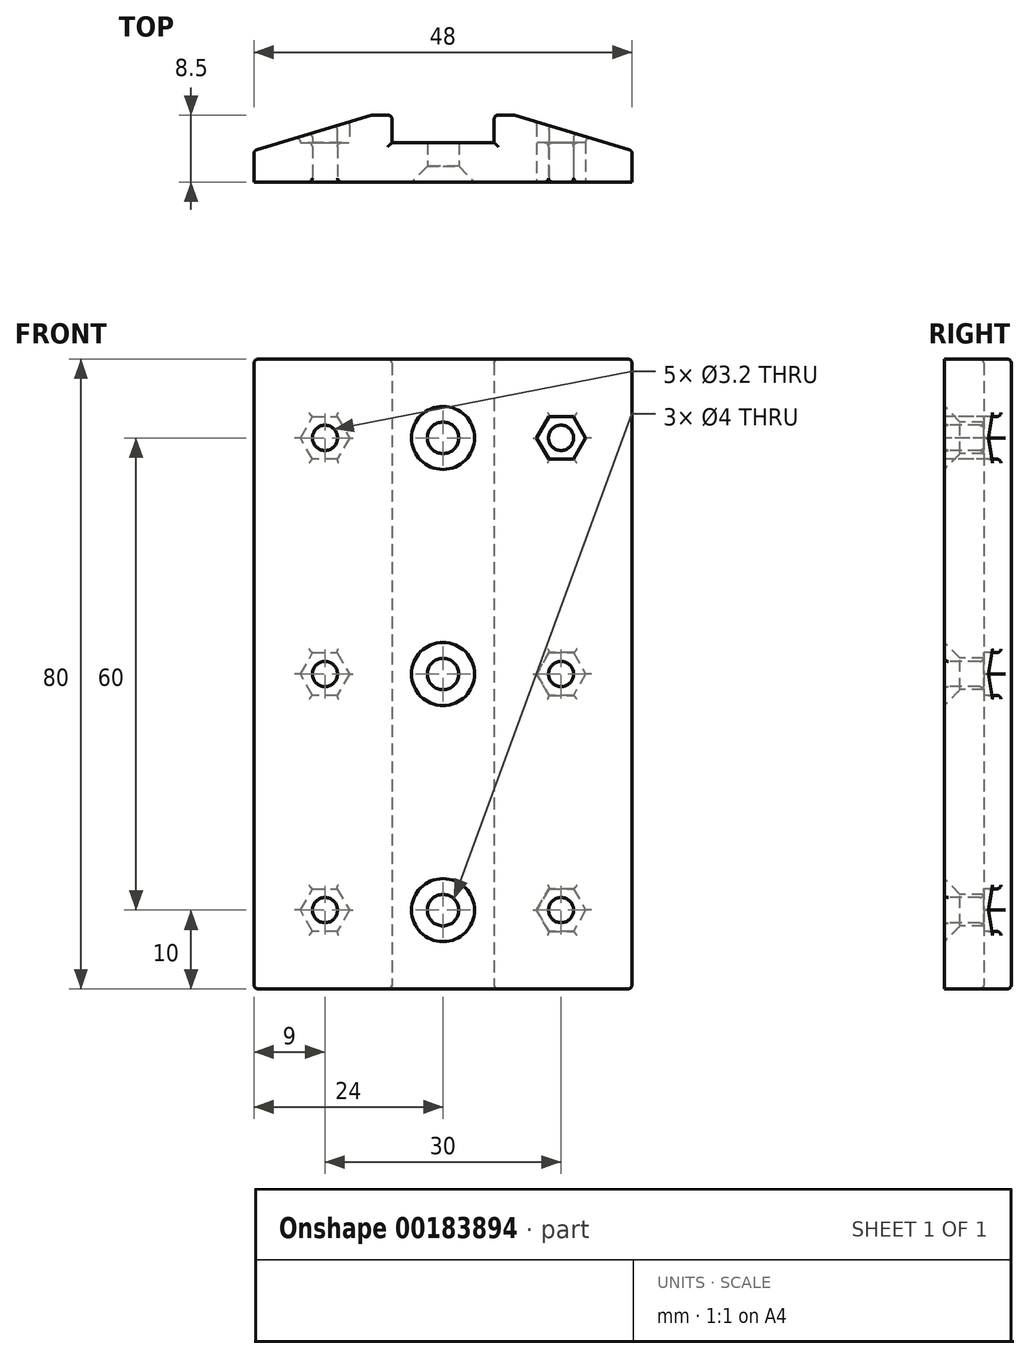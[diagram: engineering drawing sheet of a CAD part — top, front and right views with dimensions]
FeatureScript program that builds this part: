
annotation { "Feature Type Name" : "Feature", "Feature Type Description" : "" }
export const myFeature = defineFeature(function(context is Context, id is Id, definition is map)
    precondition{}
    {
        {
            var Q0;
            Q0=qCreatedBy(makeId("Front.planeOp"),FACE);
            var sketch = newSketch(context, id + "F0", { "sketchPlane" : qUnion([Q0])});
            skLineSegment(sketch, "E0.bottom", {"start": v(6, -40) * mm, "end": v(-6, -40) * mm});
            skLineSegment(sketch, "E0.top", {"start": v(6, 40) * mm, "end": v(-6, 40) * mm});
            skLineSegment(sketch, "E0.left", {"start": v(6, -40) * mm, "end": v(6, 40) * mm});
            skLineSegment(sketch, "E0.right", {"start": v(-6, -40) * mm, "end": v(-6, 40) * mm});
            skPoint(sketch, "E0.middle", {"position": v(0, 0) * mm});
            skCircle(sketch, "E1", {"center": v(0, -30) * mm, "radius": 2 * mm});
            skCircle(sketch, "E2.1.0.0", {"center": v(0, 0) * mm, "radius": 2 * mm});
            skCircle(sketch, "E2.2.0.0", {"center": v(0, 30) * mm, "radius": 2 * mm});
            skLineSegment(sketch, "E2.direction1", {"start": v(0, -30) * mm, "end": v(0, 0) * mm, "construction": true});
            skLineSegment(sketch, "E3.bottom", {"start": v(-6, 40) * mm, "end": v(-24, 40) * mm});
            skLineSegment(sketch, "E3.top", {"start": v(-6, -40) * mm, "end": v(-24, -40) * mm});
            skLineSegment(sketch, "E3.left", {"start": v(-6, 40) * mm, "end": v(-6, -40) * mm});
            skLineSegment(sketch, "E3.right", {"start": v(-24, 40) * mm, "end": v(-24, -40) * mm});
            skLineSegment(sketch, "E4.MirrorCS", {"start": v(6, 40) * mm, "end": v(24, 40) * mm});
            skLineSegment(sketch, "E5.MirrorCS", {"start": v(24, 40) * mm, "end": v(24, -40) * mm});
            skLineSegment(sketch, "E6.MirrorCS", {"start": v(6, -40) * mm, "end": v(24, -40) * mm});
            skLineSegment(sketch, "E7.0", {"start": v(-6.5, 40) * mm, "end": v(-6.5, -40) * mm});
            skLineSegment(sketch, "E8.MirrorCS", {"start": v(6.5, 40) * mm, "end": v(6.5, -40) * mm});
            skCircle(sketch, "E9", {"center": v(-15, 30) * mm, "radius": 1.6 * mm});
            skCircle(sketch, "E10.cCircle", {"center": v(-15, 30) * mm, "radius": 2.7 * mm, "construction": true});
            skLineSegment(sketch, "E10.0", {"start": v(-16.56, 32.7) * mm, "end": v(-13.44, 32.7) * mm});
            skLineSegment(sketch, "E10.1", {"start": v(-13.44, 32.7) * mm, "end": v(-11.88, 30) * mm});
            skLineSegment(sketch, "E10.2", {"start": v(-11.88, 30) * mm, "end": v(-13.44, 27.3) * mm});
            skLineSegment(sketch, "E10.3", {"start": v(-13.44, 27.3) * mm, "end": v(-16.56, 27.3) * mm});
            skLineSegment(sketch, "E10.4", {"start": v(-16.56, 27.3) * mm, "end": v(-18.12, 30) * mm});
            skLineSegment(sketch, "E10.5", {"start": v(-18.12, 30) * mm, "end": v(-16.56, 32.7) * mm});
            skPoint(sketch, "E10.0.midPoint", {"position": v(-15, 32.7) * mm});
            skLineSegment(sketch, "E11", {"start": v(-15, 40) * mm, "end": v(-15, -40) * mm, "construction": true});
            skLineSegment(sketch, "E12", {"start": v(-24, 30) * mm, "end": v(24, 30) * mm, "construction": true});
            skLineSegment(sketch, "E13", {"start": v(-24, 0) * mm, "end": v(24, 0) * mm, "construction": true});
            skLineSegment(sketch, "E14", {"start": v(-24, -30) * mm, "end": v(24, -30) * mm, "construction": true});
            skCircle(sketch, "E15.cCircle", {"center": v(-15, 0) * mm, "radius": 2.7 * mm, "construction": true});
            skLineSegment(sketch, "E15.0", {"start": v(-16.56, 2.7) * mm, "end": v(-13.44, 2.7) * mm});
            skLineSegment(sketch, "E15.1", {"start": v(-13.44, 2.7) * mm, "end": v(-11.88, 0) * mm});
            skLineSegment(sketch, "E15.2", {"start": v(-11.88, 0) * mm, "end": v(-13.44, -2.7) * mm});
            skLineSegment(sketch, "E15.3", {"start": v(-13.44, -2.7) * mm, "end": v(-16.56, -2.7) * mm});
            skLineSegment(sketch, "E15.4", {"start": v(-16.56, -2.7) * mm, "end": v(-18.12, 0) * mm});
            skLineSegment(sketch, "E15.5", {"start": v(-18.12, 0) * mm, "end": v(-16.56, 2.7) * mm});
            skPoint(sketch, "E15.0.midPoint", {"position": v(-15, 2.7) * mm});
            skCircle(sketch, "E16.cCircle", {"center": v(-15, -30) * mm, "radius": 2.7 * mm, "construction": true});
            skLineSegment(sketch, "E16.0", {"start": v(-16.56, -27.3) * mm, "end": v(-13.44, -27.3) * mm});
            skLineSegment(sketch, "E16.1", {"start": v(-13.44, -27.3) * mm, "end": v(-11.88, -30) * mm});
            skLineSegment(sketch, "E16.2", {"start": v(-11.88, -30) * mm, "end": v(-13.44, -32.7) * mm});
            skLineSegment(sketch, "E16.3", {"start": v(-13.44, -32.7) * mm, "end": v(-16.56, -32.7) * mm});
            skLineSegment(sketch, "E16.4", {"start": v(-16.56, -32.7) * mm, "end": v(-18.12, -30) * mm});
            skLineSegment(sketch, "E16.5", {"start": v(-18.12, -30) * mm, "end": v(-16.56, -27.3) * mm});
            skPoint(sketch, "E16.0.midPoint", {"position": v(-15, -27.3) * mm});
            skCircle(sketch, "E17", {"center": v(-15, 0) * mm, "radius": 1.6 * mm});
            skCircle(sketch, "E18", {"center": v(-15, -30) * mm, "radius": 1.6 * mm});
            skLineSegment(sketch, "E19", {"start": v(0, 30) * mm, "end": v(0, 0) * mm, "construction": true});
            skCircle(sketch, "E20.MirrorC", {"center": v(15, 30) * mm, "radius": 1.6 * mm});
            skLineSegment(sketch, "E21.MirrorCS", {"start": v(11.88, 30) * mm, "end": v(13.44, 27.3) * mm});
            skLineSegment(sketch, "E22.MirrorCS", {"start": v(13.44, 27.3) * mm, "end": v(16.56, 27.3) * mm});
            skLineSegment(sketch, "E23.MirrorCS", {"start": v(16.56, 27.3) * mm, "end": v(18.12, 30) * mm});
            skLineSegment(sketch, "E24.MirrorCS", {"start": v(18.12, 30) * mm, "end": v(16.56, 32.7) * mm});
            skLineSegment(sketch, "E25.MirrorCS", {"start": v(13.44, 32.7) * mm, "end": v(11.88, 30) * mm});
            skLineSegment(sketch, "E26.MirrorCS", {"start": v(16.56, 32.7) * mm, "end": v(13.44, 32.7) * mm});
            skLineSegment(sketch, "E27.MirrorCS", {"start": v(13.44, 2.7) * mm, "end": v(11.88, 0) * mm});
            skLineSegment(sketch, "E28.MirrorCS", {"start": v(16.56, 2.7) * mm, "end": v(13.44, 2.7) * mm});
            skCircle(sketch, "E29.MirrorC", {"center": v(15, 0) * mm, "radius": 1.6 * mm});
            skLineSegment(sketch, "E30.MirrorCS", {"start": v(18.12, 0) * mm, "end": v(16.56, 2.7) * mm});
            skLineSegment(sketch, "E31.MirrorCS", {"start": v(16.56, -2.7) * mm, "end": v(18.12, 0) * mm});
            skLineSegment(sketch, "E32.MirrorCS", {"start": v(13.44, -2.7) * mm, "end": v(16.56, -2.7) * mm});
            skLineSegment(sketch, "E33.MirrorCS", {"start": v(11.88, 0) * mm, "end": v(13.44, -2.7) * mm});
            skLineSegment(sketch, "E34.MirrorCS", {"start": v(11.88, -30) * mm, "end": v(13.44, -32.7) * mm});
            skLineSegment(sketch, "E35.MirrorCS", {"start": v(13.44, -27.3) * mm, "end": v(11.88, -30) * mm});
            skLineSegment(sketch, "E36.MirrorCS", {"start": v(16.56, -27.3) * mm, "end": v(13.44, -27.3) * mm});
            skLineSegment(sketch, "E37.MirrorCS", {"start": v(18.12, -30) * mm, "end": v(16.56, -27.3) * mm});
            skLineSegment(sketch, "E38.MirrorCS", {"start": v(16.56, -32.7) * mm, "end": v(18.12, -30) * mm});
            skLineSegment(sketch, "E39.MirrorCS", {"start": v(13.44, -32.7) * mm, "end": v(16.56, -32.7) * mm});
            skCircle(sketch, "E40.MirrorC", {"center": v(15, -30) * mm, "radius": 1.6 * mm});
            skSolve(sketch);
        }
        {
            var Q0;
            Q0 = qSketchRegion(id + "F0", true);
            var Q1;
            Q1=makeQuery(id+"F0.imprint","IMPRINT",FACE,{"disambiguationData":[TD([[makeQuery(id+"F0.imprint","IMPRINT",EDGE,{"derivedFrom":sQuery(id+"F0.wireOp",EDGE,"E2.2.0.0")}),1.0]])]});
            var Q2;
            Q2=makeQuery(id+"F0.imprint","IMPRINT",FACE,{"disambiguationData":[TD([[makeQuery(id+"F0.imprint","IMPRINT",EDGE,{"derivedFrom":sQuery(id+"F0.wireOp",EDGE,"E2.1.0.0")}),1.0]])]});
            var Q3;
            Q3=makeQuery(id+"F0.imprint","IMPRINT",FACE,{"disambiguationData":[TD([[makeQuery(id+"F0.imprint","IMPRINT",EDGE,{"derivedFrom":sQuery(id+"F0.wireOp",EDGE,"E1")}),1.0]])]});
            extrude(context, id + "F1", {"entities" : qUnion([Q0, Q1, Q2, Q3]), "oppositeDirection" : true, "depth" : 5 * mm});
        }
        {
            var Q0;
            {var subQ0=sQuery(id+"F0.wireOp",EDGE,"E3.right");Q0=makeQuery(id+"F0.imprint","IMPRINT",FACE,{"disambiguationData":[TD([[makeQuery(id+"F0.imprint","IMPRINT",EDGE,{"derivedFrom":subQ0}),1.0]])]});}
            var Q1;
            {var subQ0=sQuery(id+"F0.wireOp",EDGE,"E5.MirrorCS");Q1=makeQuery(id+"F0.imprint","IMPRINT",FACE,{"disambiguationData":[TD([[makeQuery(id+"F0.imprint","IMPRINT",EDGE,{"derivedFrom":subQ0}),-1.0]])]});}
            extrude(context, id + "F2", {"entities" : qUnion([Q0, Q1]), "operationType" : NewBodyOperationType.ADD, "oppositeDirection" : true, "depth" : 8.5 * mm});
        }
        {
            var Q0;
            Q0=makeQuery(id+"F2.opExtrude","CAP_EDGE",EDGE,{"disambiguationData":[OSD([sQuery(id+"F0.wireOp",EDGE,"E3.right")])],"isStart":false});
            chamfer(context, id + "F3", {"entities" : qUnion([Q0]), "chamferType" : ChamferType.TWO_OFFSETS, "width1" : 4.5 * mm, "oppositeDirection" : false, "width2" : 15 * mm});
        }
        {
            var Q0;
            Q0=makeQuery(id+"F2.opExtrude","CAP_EDGE",EDGE,{"disambiguationData":[OSD([sQuery(id+"F0.wireOp",EDGE,"E5.MirrorCS")])],"isStart":false});
            chamfer(context, id + "F4", {"entities" : qUnion([Q0]), "chamferType" : ChamferType.TWO_OFFSETS, "width1" : 4.5 * mm, "oppositeDirection" : true, "width2" : 15 * mm, "tangentPropagation" : true});
        }
        {
            var Q0;
            Q0=sQuery(id+"F0.wireOp",VERTEX,"E2.2.0.0.center");
            var Q1;
            Q1=sQuery(id+"F0.wireOp",VERTEX,"E0.middle");
            var Q2;
            Q2=sQuery(id+"F0.wireOp",VERTEX,"E2.direction1.start");
            var Q3;
            Q3=makeQuery(id+"F1.opExtrude","SWEPT_BODY",BODY,{"disambiguationData":[OSD([sQuery(id+"F0.wireOp",EDGE,"E0.bottom"),sQuery(id+"F0.wireOp",EDGE,"E0.top"),sQuery(id+"F0.wireOp",EDGE,"E3.bottom"),sQuery(id+"F0.wireOp",EDGE,"E3.top"),sQuery(id+"F0.wireOp",EDGE,"E3.right"),sQuery(id+"F0.wireOp",EDGE,"E4.MirrorCS"),sQuery(id+"F0.wireOp",EDGE,"E5.MirrorCS"),sQuery(id+"F0.wireOp",EDGE,"E6.MirrorCS")])]});
            hole(context, id + "F5", {"style" : HoleStyle.C_SINK, "endStyle" : HoleEndStyle.THROUGH, "holeDiameter" : 4 * mm, "cSinkDiameter" : 8 * mm, "cSinkAngle" : 90 * degree, "locations" : qUnion([Q0, Q1, Q2]), "scope" : qUnion([Q3]), "isTappedThrough" : true});
        }
        {
            var Q0;
            Q0=makeQuery(id+"F0.imprint","IMPRINT",FACE,{"disambiguationData":[TD([[makeQuery(id+"F0.imprint","IMPRINT",EDGE,{"derivedFrom":sQuery(id+"F0.wireOp",EDGE,"E20.MirrorC")}),1.0]])]});
            var Q1;
            Q1=makeQuery(id+"F0.imprint","IMPRINT",FACE,{"disambiguationData":[TD([[makeQuery(id+"F0.imprint","IMPRINT",EDGE,{"derivedFrom":sQuery(id+"F0.wireOp",EDGE,"E27.MirrorCS")}),1.0]])]});
            var Q2;
            Q2=makeQuery(id+"F0.imprint","IMPRINT",FACE,{"disambiguationData":[TD([[makeQuery(id+"F0.imprint","IMPRINT",EDGE,{"derivedFrom":sQuery(id+"F0.wireOp",EDGE,"E9")}),-1.0]])]});
            var Q3;
            Q3=makeQuery(id+"F0.imprint","IMPRINT",FACE,{"disambiguationData":[TD([[makeQuery(id+"F0.imprint","IMPRINT",EDGE,{"derivedFrom":sQuery(id+"F0.wireOp",EDGE,"E15.0")}),-1.0]])]});
            var Q4;
            Q4=makeQuery(id+"F0.imprint","IMPRINT",FACE,{"disambiguationData":[TD([[makeQuery(id+"F0.imprint","IMPRINT",EDGE,{"derivedFrom":sQuery(id+"F0.wireOp",EDGE,"E16.0")}),-1.0]])]});
            var Q5;
            Q5=makeQuery(id+"F0.imprint","IMPRINT",FACE,{"disambiguationData":[TD([[makeQuery(id+"F0.imprint","IMPRINT",EDGE,{"derivedFrom":sQuery(id+"F0.wireOp",EDGE,"E34.MirrorCS")}),1.0]])]});
            extrude(context, id + "F6", {"entities" : qUnion([Q0, Q1, Q2, Q3, Q4, Q5]), "operationType" : NewBodyOperationType.ADD, "oppositeDirection" : true, "depth" : 5 * mm});
        }
        {
            var Q0;
            Q0=makeQuery(id+"F4.opChamfer","BLEND_FACE",FACE,{"disambiguationData":[OSD([sQuery(id+"F0.wireOp",EDGE,"E5.MirrorCS")])]});
            var Q1;
            Q1=makeQuery(id+"F2.opExtrude","CAP_FACE",FACE,{"disambiguationData":[OSD([sQuery(id+"F0.wireOp",EDGE,"E4.MirrorCS"),sQuery(id+"F0.wireOp",EDGE,"E5.MirrorCS"),sQuery(id+"F0.wireOp",EDGE,"E6.MirrorCS"),sQuery(id+"F0.wireOp",EDGE,"E8.MirrorCS"),sQuery(id+"F0.wireOp",EDGE,"E21.MirrorCS"),sQuery(id+"F0.wireOp",EDGE,"E22.MirrorCS"),sQuery(id+"F0.wireOp",EDGE,"E23.MirrorCS"),sQuery(id+"F0.wireOp",EDGE,"E24.MirrorCS"),sQuery(id+"F0.wireOp",EDGE,"E25.MirrorCS"),sQuery(id+"F0.wireOp",EDGE,"E26.MirrorCS"),sQuery(id+"F0.wireOp",EDGE,"E27.MirrorCS"),sQuery(id+"F0.wireOp",EDGE,"E28.MirrorCS"),sQuery(id+"F0.wireOp",EDGE,"E30.MirrorCS"),sQuery(id+"F0.wireOp",EDGE,"E31.MirrorCS"),sQuery(id+"F0.wireOp",EDGE,"E32.MirrorCS"),sQuery(id+"F0.wireOp",EDGE,"E33.MirrorCS"),sQuery(id+"F0.wireOp",EDGE,"E34.MirrorCS"),sQuery(id+"F0.wireOp",EDGE,"E35.MirrorCS"),sQuery(id+"F0.wireOp",EDGE,"E36.MirrorCS"),sQuery(id+"F0.wireOp",EDGE,"E37.MirrorCS"),sQuery(id+"F0.wireOp",EDGE,"E38.MirrorCS"),sQuery(id+"F0.wireOp",EDGE,"E39.MirrorCS")])],"isStart":false});
            var Q2;
            Q2=makeQuery(id+"F2.opExtrude","CAP_FACE",FACE,{"disambiguationData":[OSD([sQuery(id+"F0.wireOp",EDGE,"E3.bottom"),sQuery(id+"F0.wireOp",EDGE,"E3.top"),sQuery(id+"F0.wireOp",EDGE,"E3.right"),sQuery(id+"F0.wireOp",EDGE,"E7.0"),sQuery(id+"F0.wireOp",EDGE,"E10.0"),sQuery(id+"F0.wireOp",EDGE,"E10.1"),sQuery(id+"F0.wireOp",EDGE,"E10.2"),sQuery(id+"F0.wireOp",EDGE,"E10.3"),sQuery(id+"F0.wireOp",EDGE,"E10.4"),sQuery(id+"F0.wireOp",EDGE,"E10.5"),sQuery(id+"F0.wireOp",EDGE,"E15.0"),sQuery(id+"F0.wireOp",EDGE,"E15.1"),sQuery(id+"F0.wireOp",EDGE,"E15.2"),sQuery(id+"F0.wireOp",EDGE,"E15.3"),sQuery(id+"F0.wireOp",EDGE,"E15.4"),sQuery(id+"F0.wireOp",EDGE,"E15.5"),sQuery(id+"F0.wireOp",EDGE,"E16.0"),sQuery(id+"F0.wireOp",EDGE,"E16.1"),sQuery(id+"F0.wireOp",EDGE,"E16.2"),sQuery(id+"F0.wireOp",EDGE,"E16.3"),sQuery(id+"F0.wireOp",EDGE,"E16.4"),sQuery(id+"F0.wireOp",EDGE,"E16.5")])],"isStart":false});
            var Q3;
            Q3=makeQuery(id+"F3.opChamfer","BLEND_FACE",FACE,{"disambiguationData":[OSD([sQuery(id+"F0.wireOp",EDGE,"E3.right")])]});
            var Q4;
            Q4=makeQuery(id+"F6.opExtrude","SWEPT_FACE",FACE,{"disambiguationData":[OSD([sQuery(id+"F0.wireOp",EDGE,"E9")])]});
            var Q5;
            Q5=makeQuery(id+"F6.opExtrude","SWEPT_FACE",FACE,{"disambiguationData":[OSD([sQuery(id+"F0.wireOp",EDGE,"E20.MirrorC")])]});
            var Q6;
            Q6=makeQuery(id+"F6.opExtrude","SWEPT_FACE",FACE,{"disambiguationData":[OSD([sQuery(id+"F0.wireOp",EDGE,"E29.MirrorC")])]});
            var Q7;
            Q7=makeQuery(id+"F6.opExtrude","SWEPT_FACE",FACE,{"disambiguationData":[OSD([sQuery(id+"F0.wireOp",EDGE,"E17")])]});
            var Q8;
            Q8=makeQuery(id+"F6.opExtrude","SWEPT_FACE",FACE,{"disambiguationData":[OSD([sQuery(id+"F0.wireOp",EDGE,"E18")])]});
            var Q9;
            Q9=makeQuery(id+"F6.opExtrude","SWEPT_FACE",FACE,{"disambiguationData":[OSD([sQuery(id+"F0.wireOp",EDGE,"E40.MirrorC")])]});
            var Q10;
            Q10=makeQuery(id+"F5.hole-2.boolean.opBoolean","INTERSECT",EDGE,{"derivedFrom":[makeQuery(id+"F1.opExtrude","CAP_FACE",FACE,{"disambiguationData":[OSD([sQuery(id+"F0.wireOp",EDGE,"E0.bottom"),sQuery(id+"F0.wireOp",EDGE,"E0.top"),sQuery(id+"F0.wireOp",EDGE,"E3.bottom"),sQuery(id+"F0.wireOp",EDGE,"E3.top"),sQuery(id+"F0.wireOp",EDGE,"E3.right"),sQuery(id+"F0.wireOp",EDGE,"E4.MirrorCS"),sQuery(id+"F0.wireOp",EDGE,"E5.MirrorCS"),sQuery(id+"F0.wireOp",EDGE,"E6.MirrorCS"),sQuery(id+"F0.wireOp",EDGE,"E10.0"),sQuery(id+"F0.wireOp",EDGE,"E10.1"),sQuery(id+"F0.wireOp",EDGE,"E10.2"),sQuery(id+"F0.wireOp",EDGE,"E10.3"),sQuery(id+"F0.wireOp",EDGE,"E10.4"),sQuery(id+"F0.wireOp",EDGE,"E10.5"),sQuery(id+"F0.wireOp",EDGE,"E15.0"),sQuery(id+"F0.wireOp",EDGE,"E15.1"),sQuery(id+"F0.wireOp",EDGE,"E15.2"),sQuery(id+"F0.wireOp",EDGE,"E15.3"),sQuery(id+"F0.wireOp",EDGE,"E15.4"),sQuery(id+"F0.wireOp",EDGE,"E15.5"),sQuery(id+"F0.wireOp",EDGE,"E16.0"),sQuery(id+"F0.wireOp",EDGE,"E16.1"),sQuery(id+"F0.wireOp",EDGE,"E16.2"),sQuery(id+"F0.wireOp",EDGE,"E16.3"),sQuery(id+"F0.wireOp",EDGE,"E16.4"),sQuery(id+"F0.wireOp",EDGE,"E16.5"),sQuery(id+"F0.wireOp",EDGE,"E21.MirrorCS"),sQuery(id+"F0.wireOp",EDGE,"E22.MirrorCS"),sQuery(id+"F0.wireOp",EDGE,"E23.MirrorCS"),sQuery(id+"F0.wireOp",EDGE,"E24.MirrorCS"),sQuery(id+"F0.wireOp",EDGE,"E25.MirrorCS"),sQuery(id+"F0.wireOp",EDGE,"E26.MirrorCS"),sQuery(id+"F0.wireOp",EDGE,"E27.MirrorCS"),sQuery(id+"F0.wireOp",EDGE,"E28.MirrorCS"),sQuery(id+"F0.wireOp",EDGE,"E30.MirrorCS"),sQuery(id+"F0.wireOp",EDGE,"E31.MirrorCS"),sQuery(id+"F0.wireOp",EDGE,"E32.MirrorCS"),sQuery(id+"F0.wireOp",EDGE,"E33.MirrorCS"),sQuery(id+"F0.wireOp",EDGE,"E34.MirrorCS"),sQuery(id+"F0.wireOp",EDGE,"E35.MirrorCS"),sQuery(id+"F0.wireOp",EDGE,"E36.MirrorCS"),sQuery(id+"F0.wireOp",EDGE,"E37.MirrorCS"),sQuery(id+"F0.wireOp",EDGE,"E38.MirrorCS"),sQuery(id+"F0.wireOp",EDGE,"E39.MirrorCS")])],"isStart":false}),makeQuery(id+"F5.hole-2.opRevolve","SWEPT_FACE",FACE,{"disambiguationData":[OSD([sQuery(id+"F5.hole-2.sketch.wireOp",EDGE,"core_line_2")])]})]});
            var Q11;
            Q11=makeQuery(id+"F5.hole-1.boolean.opBoolean","INTERSECT",EDGE,{"derivedFrom":[makeQuery(id+"F1.opExtrude","CAP_FACE",FACE,{"disambiguationData":[OSD([sQuery(id+"F0.wireOp",EDGE,"E0.bottom"),sQuery(id+"F0.wireOp",EDGE,"E0.top"),sQuery(id+"F0.wireOp",EDGE,"E3.bottom"),sQuery(id+"F0.wireOp",EDGE,"E3.top"),sQuery(id+"F0.wireOp",EDGE,"E3.right"),sQuery(id+"F0.wireOp",EDGE,"E4.MirrorCS"),sQuery(id+"F0.wireOp",EDGE,"E5.MirrorCS"),sQuery(id+"F0.wireOp",EDGE,"E6.MirrorCS"),sQuery(id+"F0.wireOp",EDGE,"E10.0"),sQuery(id+"F0.wireOp",EDGE,"E10.1"),sQuery(id+"F0.wireOp",EDGE,"E10.2"),sQuery(id+"F0.wireOp",EDGE,"E10.3"),sQuery(id+"F0.wireOp",EDGE,"E10.4"),sQuery(id+"F0.wireOp",EDGE,"E10.5"),sQuery(id+"F0.wireOp",EDGE,"E15.0"),sQuery(id+"F0.wireOp",EDGE,"E15.1"),sQuery(id+"F0.wireOp",EDGE,"E15.2"),sQuery(id+"F0.wireOp",EDGE,"E15.3"),sQuery(id+"F0.wireOp",EDGE,"E15.4"),sQuery(id+"F0.wireOp",EDGE,"E15.5"),sQuery(id+"F0.wireOp",EDGE,"E16.0"),sQuery(id+"F0.wireOp",EDGE,"E16.1"),sQuery(id+"F0.wireOp",EDGE,"E16.2"),sQuery(id+"F0.wireOp",EDGE,"E16.3"),sQuery(id+"F0.wireOp",EDGE,"E16.4"),sQuery(id+"F0.wireOp",EDGE,"E16.5"),sQuery(id+"F0.wireOp",EDGE,"E21.MirrorCS"),sQuery(id+"F0.wireOp",EDGE,"E22.MirrorCS"),sQuery(id+"F0.wireOp",EDGE,"E23.MirrorCS"),sQuery(id+"F0.wireOp",EDGE,"E24.MirrorCS"),sQuery(id+"F0.wireOp",EDGE,"E25.MirrorCS"),sQuery(id+"F0.wireOp",EDGE,"E26.MirrorCS"),sQuery(id+"F0.wireOp",EDGE,"E27.MirrorCS"),sQuery(id+"F0.wireOp",EDGE,"E28.MirrorCS"),sQuery(id+"F0.wireOp",EDGE,"E30.MirrorCS"),sQuery(id+"F0.wireOp",EDGE,"E31.MirrorCS"),sQuery(id+"F0.wireOp",EDGE,"E32.MirrorCS"),sQuery(id+"F0.wireOp",EDGE,"E33.MirrorCS"),sQuery(id+"F0.wireOp",EDGE,"E34.MirrorCS"),sQuery(id+"F0.wireOp",EDGE,"E35.MirrorCS"),sQuery(id+"F0.wireOp",EDGE,"E36.MirrorCS"),sQuery(id+"F0.wireOp",EDGE,"E37.MirrorCS"),sQuery(id+"F0.wireOp",EDGE,"E38.MirrorCS"),sQuery(id+"F0.wireOp",EDGE,"E39.MirrorCS")])],"isStart":false}),makeQuery(id+"F5.hole-1.opRevolve","SWEPT_FACE",FACE,{"disambiguationData":[OSD([sQuery(id+"F5.hole-1.sketch.wireOp",EDGE,"core_line_2")])]})]});
            var Q12;
            Q12=makeQuery(id+"F5.hole-0.boolean.opBoolean","INTERSECT",EDGE,{"derivedFrom":[makeQuery(id+"F1.opExtrude","CAP_FACE",FACE,{"disambiguationData":[OSD([sQuery(id+"F0.wireOp",EDGE,"E0.bottom"),sQuery(id+"F0.wireOp",EDGE,"E0.top"),sQuery(id+"F0.wireOp",EDGE,"E3.bottom"),sQuery(id+"F0.wireOp",EDGE,"E3.top"),sQuery(id+"F0.wireOp",EDGE,"E3.right"),sQuery(id+"F0.wireOp",EDGE,"E4.MirrorCS"),sQuery(id+"F0.wireOp",EDGE,"E5.MirrorCS"),sQuery(id+"F0.wireOp",EDGE,"E6.MirrorCS"),sQuery(id+"F0.wireOp",EDGE,"E10.0"),sQuery(id+"F0.wireOp",EDGE,"E10.1"),sQuery(id+"F0.wireOp",EDGE,"E10.2"),sQuery(id+"F0.wireOp",EDGE,"E10.3"),sQuery(id+"F0.wireOp",EDGE,"E10.4"),sQuery(id+"F0.wireOp",EDGE,"E10.5"),sQuery(id+"F0.wireOp",EDGE,"E15.0"),sQuery(id+"F0.wireOp",EDGE,"E15.1"),sQuery(id+"F0.wireOp",EDGE,"E15.2"),sQuery(id+"F0.wireOp",EDGE,"E15.3"),sQuery(id+"F0.wireOp",EDGE,"E15.4"),sQuery(id+"F0.wireOp",EDGE,"E15.5"),sQuery(id+"F0.wireOp",EDGE,"E16.0"),sQuery(id+"F0.wireOp",EDGE,"E16.1"),sQuery(id+"F0.wireOp",EDGE,"E16.2"),sQuery(id+"F0.wireOp",EDGE,"E16.3"),sQuery(id+"F0.wireOp",EDGE,"E16.4"),sQuery(id+"F0.wireOp",EDGE,"E16.5"),sQuery(id+"F0.wireOp",EDGE,"E21.MirrorCS"),sQuery(id+"F0.wireOp",EDGE,"E22.MirrorCS"),sQuery(id+"F0.wireOp",EDGE,"E23.MirrorCS"),sQuery(id+"F0.wireOp",EDGE,"E24.MirrorCS"),sQuery(id+"F0.wireOp",EDGE,"E25.MirrorCS"),sQuery(id+"F0.wireOp",EDGE,"E26.MirrorCS"),sQuery(id+"F0.wireOp",EDGE,"E27.MirrorCS"),sQuery(id+"F0.wireOp",EDGE,"E28.MirrorCS"),sQuery(id+"F0.wireOp",EDGE,"E30.MirrorCS"),sQuery(id+"F0.wireOp",EDGE,"E31.MirrorCS"),sQuery(id+"F0.wireOp",EDGE,"E32.MirrorCS"),sQuery(id+"F0.wireOp",EDGE,"E33.MirrorCS"),sQuery(id+"F0.wireOp",EDGE,"E34.MirrorCS"),sQuery(id+"F0.wireOp",EDGE,"E35.MirrorCS"),sQuery(id+"F0.wireOp",EDGE,"E36.MirrorCS"),sQuery(id+"F0.wireOp",EDGE,"E37.MirrorCS"),sQuery(id+"F0.wireOp",EDGE,"E38.MirrorCS"),sQuery(id+"F0.wireOp",EDGE,"E39.MirrorCS")])],"isStart":false}),makeQuery(id+"F5.hole-0.opRevolve","SWEPT_FACE",FACE,{"disambiguationData":[OSD([sQuery(id+"F5.hole-0.sketch.wireOp",EDGE,"core_line_2")])]})]});
            var Q13;
            Q13=makeQuery(id+"F1.opExtrude","CAP_EDGE",EDGE,{"disambiguationData":[OSD([sQuery(id+"F0.wireOp",EDGE,"E0.top"),sQuery(id+"F0.wireOp",EDGE,"E3.bottom"),sQuery(id+"F0.wireOp",EDGE,"E4.MirrorCS")])],"isStart":false});
            var Q14;
            Q14=makeQuery(id+"F2.opExtrude","SWEPT_EDGE",EDGE,{"disambiguationData":[OSD([sQuery(id+"F0.wireOp",EDGE,"E4.MirrorCS"),sQuery(id+"F0.wireOp",EDGE,"E8.MirrorCS")])]});
            var Q15;
            Q15=makeQuery(id+"F2.opExtrude","SWEPT_EDGE",EDGE,{"disambiguationData":[OSD([sQuery(id+"F0.wireOp",EDGE,"E3.bottom"),sQuery(id+"F0.wireOp",EDGE,"E7.0")])]});
            var Q16;
            Q16=makeQuery(id+"F1.opExtrude","CAP_EDGE",EDGE,{"disambiguationData":[OSD([sQuery(id+"F0.wireOp",EDGE,"E0.bottom"),sQuery(id+"F0.wireOp",EDGE,"E3.top"),sQuery(id+"F0.wireOp",EDGE,"E6.MirrorCS")])],"isStart":false});
            var Q17;
            Q17=makeQuery(id+"F2.opExtrude","SWEPT_EDGE",EDGE,{"disambiguationData":[OSD([sQuery(id+"F0.wireOp",EDGE,"E3.top"),sQuery(id+"F0.wireOp",EDGE,"E7.0")])]});
            var Q18;
            Q18=makeQuery(id+"F2.opExtrude","SWEPT_EDGE",EDGE,{"disambiguationData":[OSD([sQuery(id+"F0.wireOp",EDGE,"E6.MirrorCS"),sQuery(id+"F0.wireOp",EDGE,"E8.MirrorCS")])]});
            var Q19;
            {var subQ0=sQuery(id+"F0.wireOp",EDGE,"E3.right");var subQ1=sQuery(id+"F0.wireOp",EDGE,"E3.top");Q19=makeQuery(id+"F2.boolean.opBoolean","MERGE",EDGE,{"derivedFrom":[makeQuery(id+"F1.opExtrude","SWEPT_EDGE",EDGE,{"disambiguationData":[OSD([subQ1,subQ0])]}),makeQuery(id+"F2.opExtrude","SWEPT_EDGE",EDGE,{"disambiguationData":[OSD([subQ1,subQ0])]})]});}
            var Q20;
            {var subQ0=sQuery(id+"F0.wireOp",EDGE,"E6.MirrorCS");var subQ1=sQuery(id+"F0.wireOp",EDGE,"E5.MirrorCS");Q20=makeQuery(id+"F2.boolean.opBoolean","MERGE",EDGE,{"derivedFrom":[makeQuery(id+"F1.opExtrude","SWEPT_EDGE",EDGE,{"disambiguationData":[OSD([subQ1,subQ0])]}),makeQuery(id+"F2.opExtrude","SWEPT_EDGE",EDGE,{"disambiguationData":[OSD([subQ1,subQ0])]})]});}
            var Q21;
            {var subQ0=sQuery(id+"F0.wireOp",EDGE,"E5.MirrorCS");var subQ1=sQuery(id+"F0.wireOp",EDGE,"E4.MirrorCS");Q21=makeQuery(id+"F2.boolean.opBoolean","MERGE",EDGE,{"derivedFrom":[makeQuery(id+"F1.opExtrude","SWEPT_EDGE",EDGE,{"disambiguationData":[OSD([subQ1,subQ0])]}),makeQuery(id+"F2.opExtrude","SWEPT_EDGE",EDGE,{"disambiguationData":[OSD([subQ1,subQ0])]})]});}
            var Q22;
            {var subQ0=sQuery(id+"F0.wireOp",EDGE,"E3.right");var subQ1=sQuery(id+"F0.wireOp",EDGE,"E3.bottom");Q22=makeQuery(id+"F2.boolean.opBoolean","MERGE",EDGE,{"derivedFrom":[makeQuery(id+"F1.opExtrude","SWEPT_EDGE",EDGE,{"disambiguationData":[OSD([subQ1,subQ0])]}),makeQuery(id+"F2.opExtrude","SWEPT_EDGE",EDGE,{"disambiguationData":[OSD([subQ1,subQ0])]})]});}
            fillet(context, id + "F7", {"entities" : qUnion([Q0, Q1, Q2, Q3, Q4, Q5, Q6, Q7, Q8, Q9, Q10, Q11, Q12, Q13, Q14, Q15, Q16, Q17, Q18, Q19, Q20, Q21, Q22]), "radius" : 0.5 * mm, "tangentPropagation" : true, "allowEdgeOverflow" : false});
        }
    });
